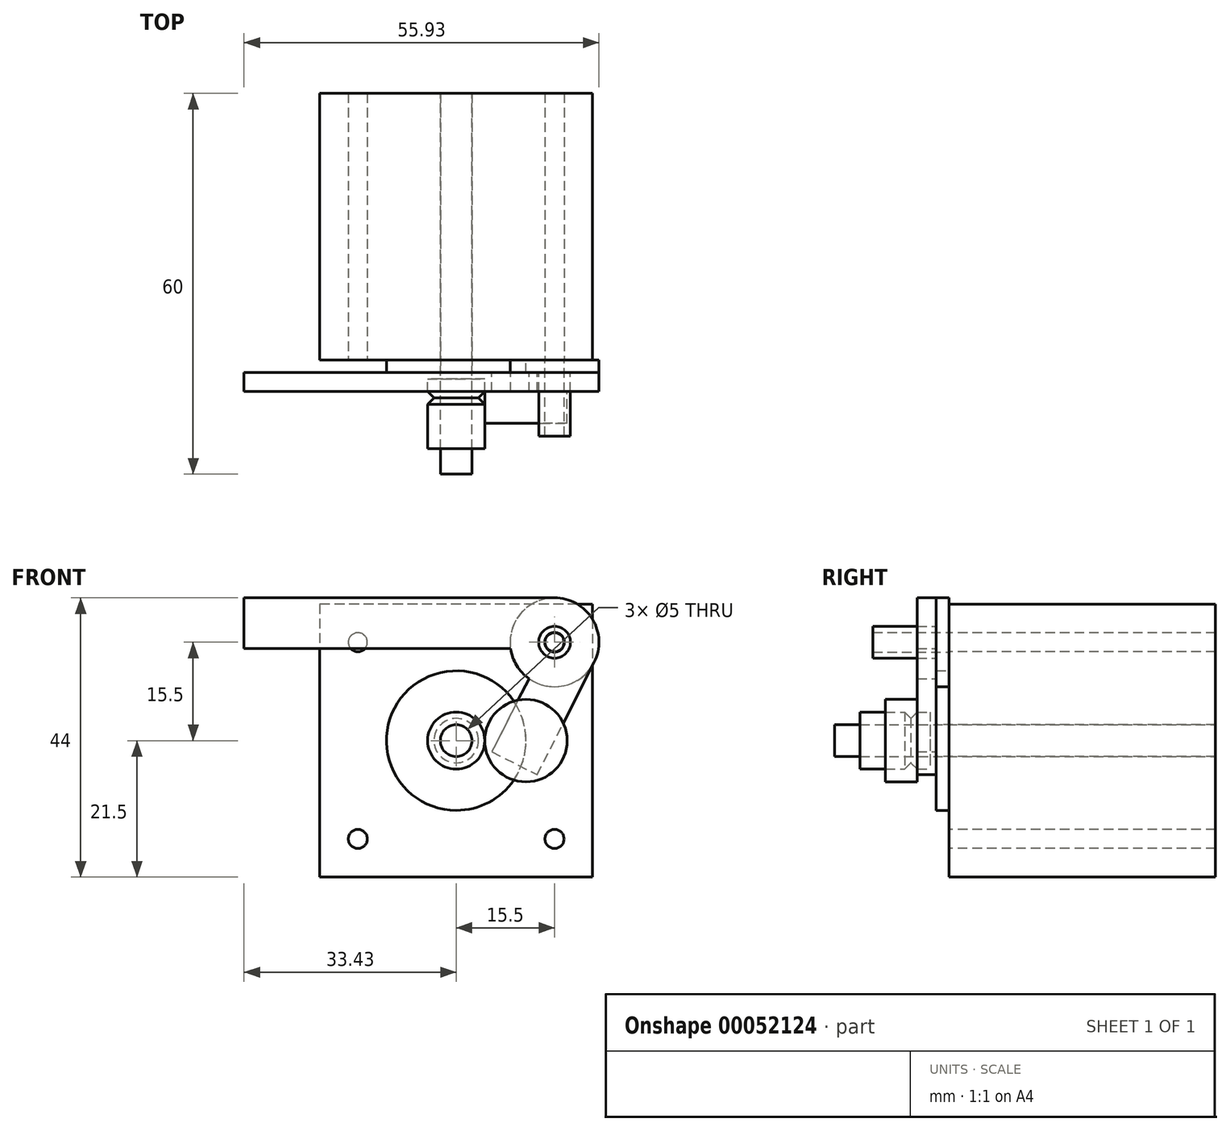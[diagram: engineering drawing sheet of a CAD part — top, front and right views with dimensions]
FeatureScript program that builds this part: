
annotation { "Feature Type Name" : "Feature", "Feature Type Description" : "" }
export const myFeature = defineFeature(function(context is Context, id is Id, definition is map)
    precondition{}
    {
        {
            var Q0;
            Q0=qCreatedBy(makeId("Front.planeOp"),FACE);
            var sketch = newSketch(context, id + "F0", { "sketchPlane" : qUnion([Q0])});
            skLineSegment(sketch, "E0.rect.bottom", {"start": v(21.5, 21.5) * mm, "end": v(-21.5, 21.5) * mm});
            skLineSegment(sketch, "E0.rect.top", {"start": v(21.5, -21.5) * mm, "end": v(-21.5, -21.5) * mm});
            skLineSegment(sketch, "E0.rect.left", {"start": v(21.5, 21.5) * mm, "end": v(21.5, -21.5) * mm});
            skLineSegment(sketch, "E0.rect.right", {"start": v(-21.5, 21.5) * mm, "end": v(-21.5, -21.5) * mm});
            skPoint(sketch, "E0.rect.middle", {"position": v(0, 0) * mm});
            skPoint(sketch, "E1", {"position": v(-15.5, 15.5) * mm});
            skPoint(sketch, "E2", {"position": v(-15.5, -15.5) * mm});
            skPoint(sketch, "E3", {"position": v(15.5, -15.5) * mm});
            skPoint(sketch, "E4", {"position": v(15.5, 15.5) * mm});
            skCircle(sketch, "E5", {"center": v(0, 0) * mm, "radius": 2.5 * mm});
            skSolve(sketch);
        }
        {
            var Q0;
            Q0=makeQuery(id+"F0.imprint","IMPRINT",FACE,{"disambiguationData":[TD([[makeQuery(id+"F0.imprint","IMPRINT",EDGE,{"derivedFrom":sQuery(id+"F0.wireOp",EDGE,"E0.rect.bottom")}),1.0]])]});
            extrude(context, id + "F1", {"entities" : qUnion([Q0]), "oppositeDirection" : true, "depth" : 42 * mm});
        }
        {
            var Q0;
            Q0=makeQuery(id+"F1.opExtrude","CAP_FACE",FACE,{"disambiguationData":[OSD([sQuery(id+"F0.wireOp",EDGE,"E0.rect.bottom"),sQuery(id+"F0.wireOp",EDGE,"E0.rect.top"),sQuery(id+"F0.wireOp",EDGE,"E0.rect.left"),sQuery(id+"F0.wireOp",EDGE,"E0.rect.right"),sQuery(id+"F0.wireOp",EDGE,"E5")])],"isStart":true});
            var sketch = newSketch(context, id + "F2", { "sketchPlane" : qUnion([Q0])});
            skCircle(sketch, "E6", {"center": v(0, 0) * mm, "radius": 11 * mm});
            skCircle(sketch, "E7", {"center": v(0, 0) * mm, "radius": 2.5 * mm});
            skSolve(sketch);
        }
        {
            var Q0;
            Q0 = qSketchRegion(id + "F2", true);
            extrude(context, id + "F3", {"entities" : qUnion([Q0]), "operationType" : NewBodyOperationType.ADD, "depth" : 2 * mm});
        }
        {
            var Q0;
            Q0=sQuery(id+"F0.wireOp",VERTEX,"E1");
            var Q1;
            Q1=sQuery(id+"F0.wireOp",VERTEX,"E4");
            var Q2;
            Q2=sQuery(id+"F0.wireOp",VERTEX,"E3");
            var Q3;
            Q3=sQuery(id+"F0.wireOp",VERTEX,"E2");
            var Q4;
            Q4=makeQuery(id+"F1.opExtrude","SWEPT_BODY",BODY,{"disambiguationData":[OSD([sQuery(id+"F0.wireOp",EDGE,"E0.rect.bottom"),sQuery(id+"F0.wireOp",EDGE,"E0.rect.top"),sQuery(id+"F0.wireOp",EDGE,"E0.rect.left"),sQuery(id+"F0.wireOp",EDGE,"E0.rect.right"),sQuery(id+"F0.wireOp",EDGE,"E5")])]});
            hole(context, id + "F4", {"style" : HoleStyle.SIMPLE, "holeDiameter" : 3 * mm, "endStyle" : HoleEndStyle.THROUGH, "locations" : qUnion([Q0, Q1, Q2, Q3]), "scope" : qUnion([Q4])});
        }
        {
            var Q0;
            Q0=makeQuery(id+"F1.opExtrude","CAP_FACE",FACE,{"disambiguationData":[OSD([sQuery(id+"F0.wireOp",EDGE,"E0.rect.bottom"),sQuery(id+"F0.wireOp",EDGE,"E0.rect.top"),sQuery(id+"F0.wireOp",EDGE,"E0.rect.left"),sQuery(id+"F0.wireOp",EDGE,"E0.rect.right"),sQuery(id+"F0.wireOp",EDGE,"E5")])],"isStart":false});
            var sketch = newSketch(context, id + "F5", { "sketchPlane" : qUnion([Q0])});
            skCircle(sketch, "E8", {"center": v(0, 0) * mm, "radius": 2.5 * mm});
            skSolve(sketch);
        }
        {
            var Q0;
            Q0 = qSketchRegion(id + "F5", true);
            extrude(context, id + "F6", {"entities" : qUnion([Q0]), "oppositeDirection" : true, "depth" : 60 * mm});
        }
        {
            var Q0;
            Q0=makeQuery(id+"F3.opExtrude","CAP_FACE",FACE,{"disambiguationData":[OSD([sQuery(id+"F2.wireOp",EDGE,"E6"),sQuery(id+"F2.wireOp",EDGE,"E7")])],"isStart":false});
            cPlane(context, id + "F7", {"entities" : qUnion([Q0]), "cplaneType" : CPlaneType.OFFSET, "offset" : 1 * mm, "width" : 150 * mm, "height" : 150 * mm});
        }
        {
            var Q0;
            Q0=qCreatedBy(id+"F7.planeOp",FACE);
            var sketch = newSketch(context, id + "F8", { "sketchPlane" : qUnion([Q0])});
            skCircle(sketch, "E9", {"center": v(0, 0) * mm, "radius": 2.5 * mm});
            skCircle(sketch, "E10", {"center": v(0, 0) * mm, "radius": 4.5 * mm});
            skSolve(sketch);
        }
        {
            var Q0;
            Q0=qCreatedBy(makeId("Right.planeOp"),FACE);
            var sketch = newSketch(context, id + "F9", { "sketchPlane" : qUnion([Q0])});
            skLineSegment(sketch, "E11", {"start": v(-3, 2.5) * mm, "end": v(-14, 2.5) * mm});
            skLineSegment(sketch, "E12", {"start": v(-14, 2.5) * mm, "end": v(-14, 4.5) * mm});
            skLineSegment(sketch, "E13", {"start": v(-14, 4.5) * mm, "end": v(-7, 4.5) * mm});
            skLineSegment(sketch, "E14", {"start": v(-6, 3.5) * mm, "end": v(-7, 4.5) * mm});
            skLineSegment(sketch, "E15", {"start": v(-5, 4.5) * mm, "end": v(-6, 3.5) * mm});
            skLineSegment(sketch, "E16", {"start": v(-5, 4.5) * mm, "end": v(-3, 4.5) * mm});
            skLineSegment(sketch, "E17", {"start": v(-3, 4.5) * mm, "end": v(-3, 2.5) * mm});
            skSolve(sketch);
        }
        {
            var Q0;
            Q0 = qSketchRegion(id + "F9", true);
            var Q1;
            Q1=makeQuery(id+"F6.opExtrude","CAP_EDGE",EDGE,{"disambiguationData":[OSD([sQuery(id+"F5.wireOp",EDGE,"E8")])],"isStart":false});
            revolve(context, id + "F10", {"entities" : qUnion([Q0]), "axis" : qUnion([Q1]), "revolveType" : RevolveType.FULL});
        }
        {
            var Q0;
            Q0=makeQuery(id+"F1.opExtrude","CAP_FACE",FACE,{"disambiguationData":[OSD([sQuery(id+"F0.wireOp",EDGE,"E0.rect.bottom"),sQuery(id+"F0.wireOp",EDGE,"E0.rect.top"),sQuery(id+"F0.wireOp",EDGE,"E0.rect.left"),sQuery(id+"F0.wireOp",EDGE,"E0.rect.right"),sQuery(id+"F0.wireOp",EDGE,"E5")])],"isStart":true});
            var sketch = newSketch(context, id + "F11", { "sketchPlane" : qUnion([Q0])});
            skCircle(sketch, "E18", {"center": v(15.5, 15.5) * mm, "radius": 7 * mm});
            skCircle(sketch, "E19", {"center": v(15.5, 15.5) * mm, "radius": 1.55 * mm});
            skSolve(sketch);
        }
        {
            var Q0;
            Q0 = qSketchRegion(id + "F11", true);
            extrude(context, id + "F12", {"entities" : qUnion([Q0]), "depth" : 2 * mm});
        }
        {
            var Q0;
            Q0=makeQuery(id+"F12.opExtrude","CAP_FACE",FACE,{"disambiguationData":[OSD([sQuery(id+"F11.wireOp",EDGE,"E18"),sQuery(id+"F11.wireOp",EDGE,"E19")])],"isStart":false});
            var sketch = newSketch(context, id + "F13", { "sketchPlane" : qUnion([Q0])});
            skCircle(sketch, "E20", {"center": v(15.5, 15.5) * mm, "radius": 2.5 * mm});
            skSolve(sketch);
        }
        {
            var Q0;
            Q0=makeQuery(id+"F13.imprint","IMPRINT",FACE,{"disambiguationData":[TD([[makeQuery(id+"F13.imprint","IMPRINT",EDGE,{"derivedFrom":sQuery(id+"F13.wireOp",EDGE,"E20")}),1.0]])]});
            extrude(context, id + "F14", {"entities" : qUnion([Q0]), "operationType" : NewBodyOperationType.ADD, "depth" : 10 * mm});
        }
        {
            var Q0;
            Q0=makeQuery(id+"F12.opExtrude","CAP_FACE",FACE,{"disambiguationData":[OSD([sQuery(id+"F11.wireOp",EDGE,"E18"),sQuery(id+"F11.wireOp",EDGE,"E19")])],"isStart":false});
            var sketch = newSketch(context, id + "F15", { "sketchPlane" : qUnion([Q0])});
            skCircle(sketch, "E21", {"center": v(15.5, 15.5) * mm, "radius": 7 * mm});
            skLineSegment(sketch, "E22", {"start": v(15.5, 22.5) * mm, "end": v(-33.43, 22.5) * mm});
            skLineSegment(sketch, "E23", {"start": v(-33.43, 22.5) * mm, "end": v(-33.43, 14.5) * mm});
            skLineSegment(sketch, "E24", {"start": v(-33.43, 14.5) * mm, "end": v(8.57, 14.5) * mm});
            skPoint(sketch, "E25", {"position": v(11, 0) * mm});
            skLineSegment(sketch, "E26", {"start": v(11.47, 9.77) * mm, "end": v(7.43, 1.8) * mm});
            skLineSegment(sketch, "E27", {"start": v(7.43, 1.8) * mm, "end": v(11, 0) * mm, "construction": true});
            skLineSegment(sketch, "E28", {"start": v(11, 0) * mm, "end": v(14.57, -1.8) * mm, "construction": true});
            skLineSegment(sketch, "E29", {"start": v(14.57, -1.8) * mm, "end": v(21.74, 12.33) * mm});
            skLineSegment(sketch, "E30", {"start": v(7.43, 1.8) * mm, "end": v(5.62, -1.76) * mm});
            skLineSegment(sketch, "E31", {"start": v(5.62, -1.76) * mm, "end": v(12.76, -5.38) * mm});
            skLineSegment(sketch, "E32", {"start": v(12.76, -5.38) * mm, "end": v(14.57, -1.8) * mm});
            skCircle(sketch, "E33", {"center": v(11, 0) * mm, "radius": 6.5 * mm, "construction": true});
            skCircle(sketch, "E34", {"center": v(15.5, 15.5) * mm, "radius": 2.5 * mm});
            skSolve(sketch);
        }
        {
            var Q0;
            Q0 = qSketchRegion(id + "F15", true);
            extrude(context, id + "F16", {"entities" : qUnion([Q0]), "depth" : 3 * mm});
        }
        {
            var Q0;
            Q0=makeQuery(id+"F16.opExtrude","CAP_FACE",FACE,{"disambiguationData":[OSD([sQuery(id+"F15.wireOp",EDGE,"E21"),sQuery(id+"F15.wireOp",EDGE,"E22"),sQuery(id+"F15.wireOp",EDGE,"E23"),sQuery(id+"F15.wireOp",EDGE,"E24"),sQuery(id+"F15.wireOp",EDGE,"E26"),sQuery(id+"F15.wireOp",EDGE,"E29"),sQuery(id+"F15.wireOp",EDGE,"E30"),sQuery(id+"F15.wireOp",EDGE,"E31"),sQuery(id+"F15.wireOp",EDGE,"E32"),sQuery(id+"F15.wireOp",EDGE,"E34")])],"isStart":false});
            var sketch = newSketch(context, id + "F17", { "sketchPlane" : qUnion([Q0])});
            skCircle(sketch, "E35", {"center": v(11, 0) * mm, "radius": 6.5 * mm});
            skSolve(sketch);
        }
        {
            var Q0;
            Q0 = qSketchRegion(id + "F17", true);
            extrude(context, id + "F18", {"entities" : qUnion([Q0]), "depth" : 5 * mm});
        }
    });
